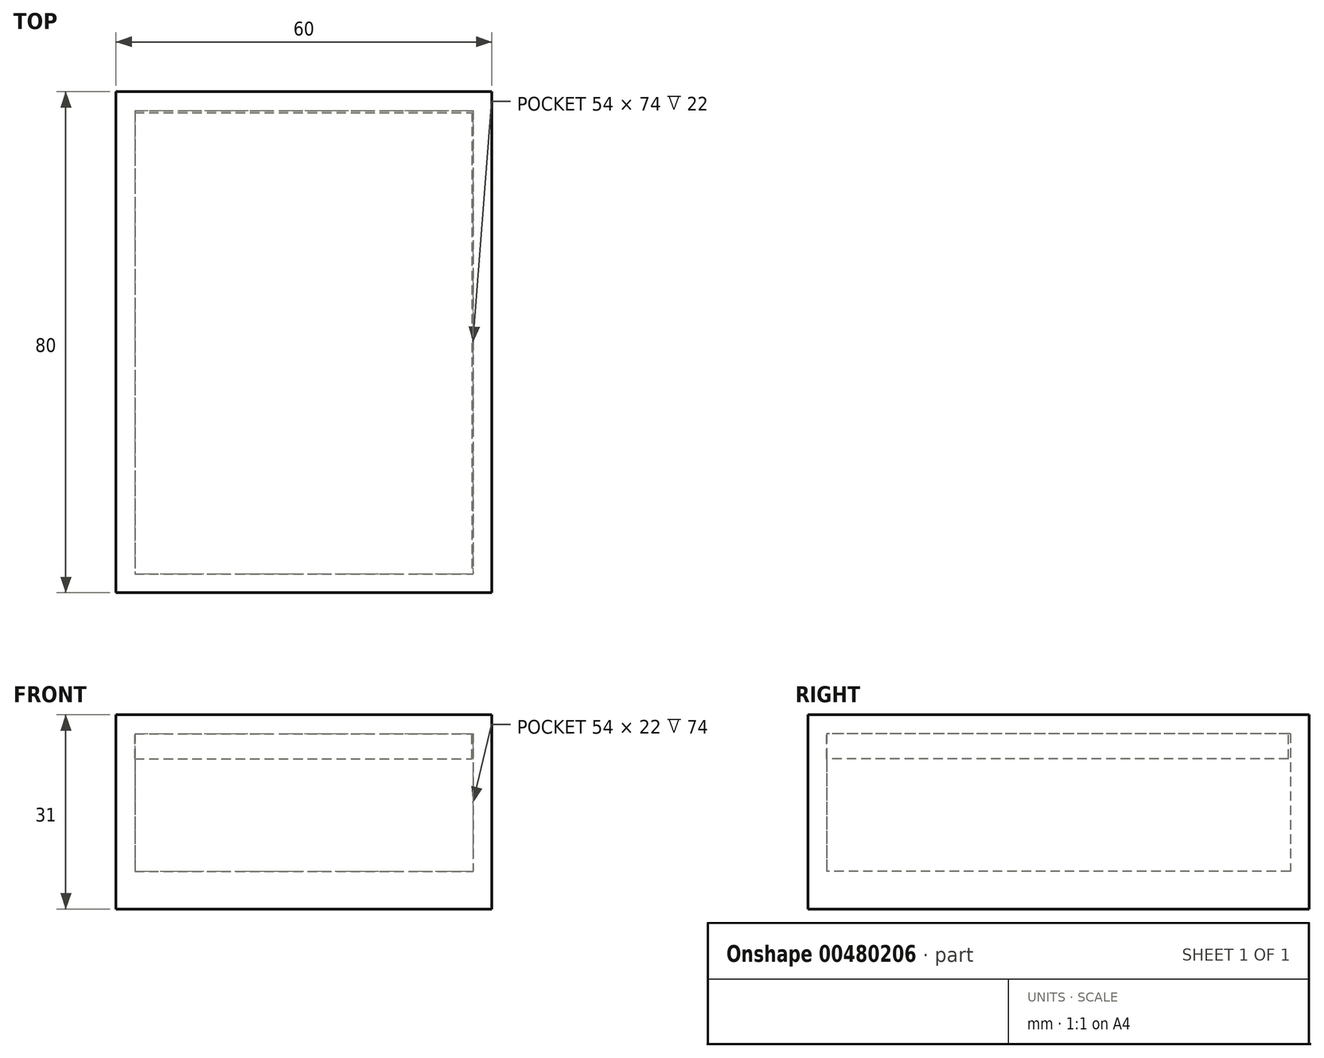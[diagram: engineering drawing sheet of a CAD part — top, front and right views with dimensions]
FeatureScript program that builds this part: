
annotation { "Feature Type Name" : "Feature", "Feature Type Description" : "" }
export const myFeature = defineFeature(function(context is Context, id is Id, definition is map)
    precondition{}
    {
        {
            var Q0;
            Q0=qCreatedBy(makeId("Top.planeOp"),FACE);
            var sketch = newSketch(context, id + "F0", { "sketchPlane" : qUnion([Q0])});
            skLineSegment(sketch, "E0.bottom", {"start": v(-30, 40) * mm, "end": v(30, 40) * mm});
            skLineSegment(sketch, "E0.top", {"start": v(-30, -40) * mm, "end": v(30, -40) * mm});
            skLineSegment(sketch, "E0.left", {"start": v(-30, 40) * mm, "end": v(-30, -40) * mm});
            skLineSegment(sketch, "E0.right", {"start": v(30, 40) * mm, "end": v(30, -40) * mm});
            skPoint(sketch, "E0.middle", {"position": v(0, 0) * mm});
            skSolve(sketch);
        }
        {
            var Q0;
            Q0=makeQuery(id+"F0.imprint","IMPRINT",FACE,{"disambiguationData":[TD([[makeQuery(id+"F0.imprint","IMPRINT",EDGE,{"derivedFrom":sQuery(id+"F0.wireOp",EDGE,"E0.bottom")}),-1.0]])]});
            extrude(context, id + "F1", {"entities" : qUnion([Q0]), "depth" : 25 * mm});
        }
        {
            var Q0;
            Q0=makeQuery(id+"F1.opExtrude","CAP_FACE",FACE,{"disambiguationData":[OSD([sQuery(id+"F0.wireOp",EDGE,"E0.bottom"),sQuery(id+"F0.wireOp",EDGE,"E0.top"),sQuery(id+"F0.wireOp",EDGE,"E0.left"),sQuery(id+"F0.wireOp",EDGE,"E0.right")])],"isStart":false});
            shell(context, id + "F2", {"entities" : qUnion([Q0]), "thickness" : 3 * mm});
        }
        {
            var Q0;
            Q0=makeQuery(id+"F1.opExtrude","CAP_FACE",FACE,{"disambiguationData":[OSD([sQuery(id+"F0.wireOp",EDGE,"E0.bottom"),sQuery(id+"F0.wireOp",EDGE,"E0.top"),sQuery(id+"F0.wireOp",EDGE,"E0.left"),sQuery(id+"F0.wireOp",EDGE,"E0.right")])],"isStart":false});
            var sketch = newSketch(context, id + "F3", { "sketchPlane" : qUnion([Q0])});
            skSolve(sketch);
        }
        {
            var Q0;
            Q0=makeQuery(id+"F1.opExtrude","CAP_FACE",FACE,{"disambiguationData":[OSD([sQuery(id+"F0.wireOp",EDGE,"E0.bottom"),sQuery(id+"F0.wireOp",EDGE,"E0.top"),sQuery(id+"F0.wireOp",EDGE,"E0.left"),sQuery(id+"F0.wireOp",EDGE,"E0.right")])],"isStart":true});
            extrude(context, id + "F4", {"entities" : qUnion([Q0]), "operationType" : NewBodyOperationType.ADD, "depth" : 3 * mm});
        }
        {
            var Q0;
            {var subQ6=sQuery(id+"F0.wireOp",EDGE,"E0.bottom");var subQ7=makeQuery(id+"F1.opExtrude","CAP_EDGE",EDGE,{"disambiguationData":[OSD([subQ6])],"isStart":false});Q0=makeQuery(id+"F3.imprint","IMPRINT",FACE,{"disambiguationData":[TD([[makeQuery(id+"F3.imprint","IMPRINT",EDGE,{"derivedFrom":subQ7}),-1.0]])]});}
            var sketch = newSketch(context, id + "F5", { "sketchPlane" : qUnion([Q0])});
            skLineSegment(sketch, "E1.bottom", {"start": v(-29.85, 40.17) * mm, "end": v(29.9, 40.17) * mm});
            skLineSegment(sketch, "E1.top", {"start": v(-29.85, -39.93) * mm, "end": v(29.9, -39.93) * mm});
            skLineSegment(sketch, "E1.left", {"start": v(-29.85, 40.17) * mm, "end": v(-29.85, -39.93) * mm});
            skLineSegment(sketch, "E1.right", {"start": v(29.9, 40.17) * mm, "end": v(29.9, -39.93) * mm});
            skLineSegment(sketch, "E2.bottom", {"start": v(-27.03, 36.7) * mm, "end": v(26.79, 36.7) * mm});
            skLineSegment(sketch, "E2.top", {"start": v(-27.03, -37.31) * mm, "end": v(26.79, -37.31) * mm});
            skLineSegment(sketch, "E2.left", {"start": v(-27.03, 36.7) * mm, "end": v(-27.03, -37.31) * mm});
            skLineSegment(sketch, "E2.right", {"start": v(26.79, 36.7) * mm, "end": v(26.79, -37.31) * mm});
            skSolve(sketch);
        }
        {
            var Q0;
            {var subQ6=sQuery(id+"F0.wireOp",EDGE,"E0.bottom");var subQ7=makeQuery(id+"F1.opExtrude","CAP_EDGE",EDGE,{"disambiguationData":[OSD([subQ6])],"isStart":false});Q0=makeQuery(id+"F3.imprint","IMPRINT",FACE,{"disambiguationData":[TD([[makeQuery(id+"F3.imprint","IMPRINT",EDGE,{"derivedFrom":subQ7}),-1.0]])]});}
            var Q1;
            {var subQ0=sQuery(id+"F0.wireOp",EDGE,"E0.bottom");Q1=makeQuery(id+"F3.imprint","IMPRINT",FACE,{"disambiguationData":[TD([[makeQuery(id+"F3.imprint","IMPRINT",EDGE,{"derivedFrom":makeQuery(id+"F2.opShell","OFFSET_EDGE",EDGE,{"disambiguationData":[OSD([subQ0]),TDD([makeQuery(id+"F1.opExtrude","CAP_EDGE",EDGE,{"disambiguationData":[OSD([subQ0])],"isStart":false})])]})}),-1.0]])]});}
            extrude(context, id + "F6", {"entities" : qUnion([Q0, Q1]), "depth" : 3 * mm});
        }
        {
            var Q0;
            {var subQ0=sQuery(id+"F5.wireOp",EDGE,"E2.right");var subQ1=sQuery(id+"F5.wireOp",EDGE,"E2.bottom");var subQ2=makeQuery(id+"F5.imprint","INTERSECT",VERTEX,{"derivedFrom":[subQ1,subQ0]});Q0=makeQuery(id+"F5.imprint","IMPRINT",FACE,{"disambiguationData":[TD([[makeQuery(id+"F5.imprint","IMPRINT",EDGE,{"disambiguationData":[TD([[subQ2,1.0]])],"derivedFrom":subQ1}),-1.0]])]});}
            extrude(context, id + "F7", {"entities" : qUnion([Q0]), "operationType" : NewBodyOperationType.ADD, "oppositeDirection" : true, "depth" : 4 * mm});
        }
        {
            var Q0;
            Q0=makeQuery(id+"F7.opExtrude","CAP_FACE",FACE,{"disambiguationData":[OSD([sQuery(id+"F0.wireOp",EDGE,"E0.top"),sQuery(id+"F0.wireOp",EDGE,"E0.left"),sQuery(id+"F5.wireOp",EDGE,"E2.bottom"),sQuery(id+"F5.wireOp",EDGE,"E2.right")])],"isStart":false});
            var sketch = newSketch(context, id + "F8", { "sketchPlane" : qUnion([Q0])});
            skCircle(sketch, "E3", {"center": v(17.31, -18.5) * mm, "radius": 7.3 * mm});
            skCircle(sketch, "E4", {"center": v(17.31, -18.5) * mm, "radius": 4.05 * mm});
            skCircle(sketch, "E5", {"center": v(-13.24, -21.96) * mm, "radius": 6.27 * mm});
            skCircle(sketch, "E6", {"center": v(-13.24, -21.96) * mm, "radius": 2.95 * mm});
            skCircle(sketch, "E7", {"center": v(11.97, 12.5) * mm, "radius": 5.96 * mm});
            skCircle(sketch, "E8", {"center": v(11.97, 12.5) * mm, "radius": 3.44 * mm});
            skCircle(sketch, "E9", {"center": v(-12.77, 9.62) * mm, "radius": 6.43 * mm});
            skCircle(sketch, "E10", {"center": v(-12.77, 9.62) * mm, "radius": 3.95 * mm});
            skSolve(sketch);
        }
        {
            var Q0;
            Q0=sQuery(id+"F8.wireOp",EDGE,"E3");
            var Q1;
            Q1=sQuery(id+"F8.wireOp",EDGE,"E5");
            var Q2;
            Q2=sQuery(id+"F8.wireOp",EDGE,"E7");
            var Q3;
            Q3=sQuery(id+"F8.wireOp",EDGE,"E9");
            extrude(context, id + "F9", {"bodyType" : ToolBodyType.SURFACE, "surfaceEntities" : qUnion([Q0, Q1, Q2, Q3]), "depth" : 10 * mm});
        }
    });
